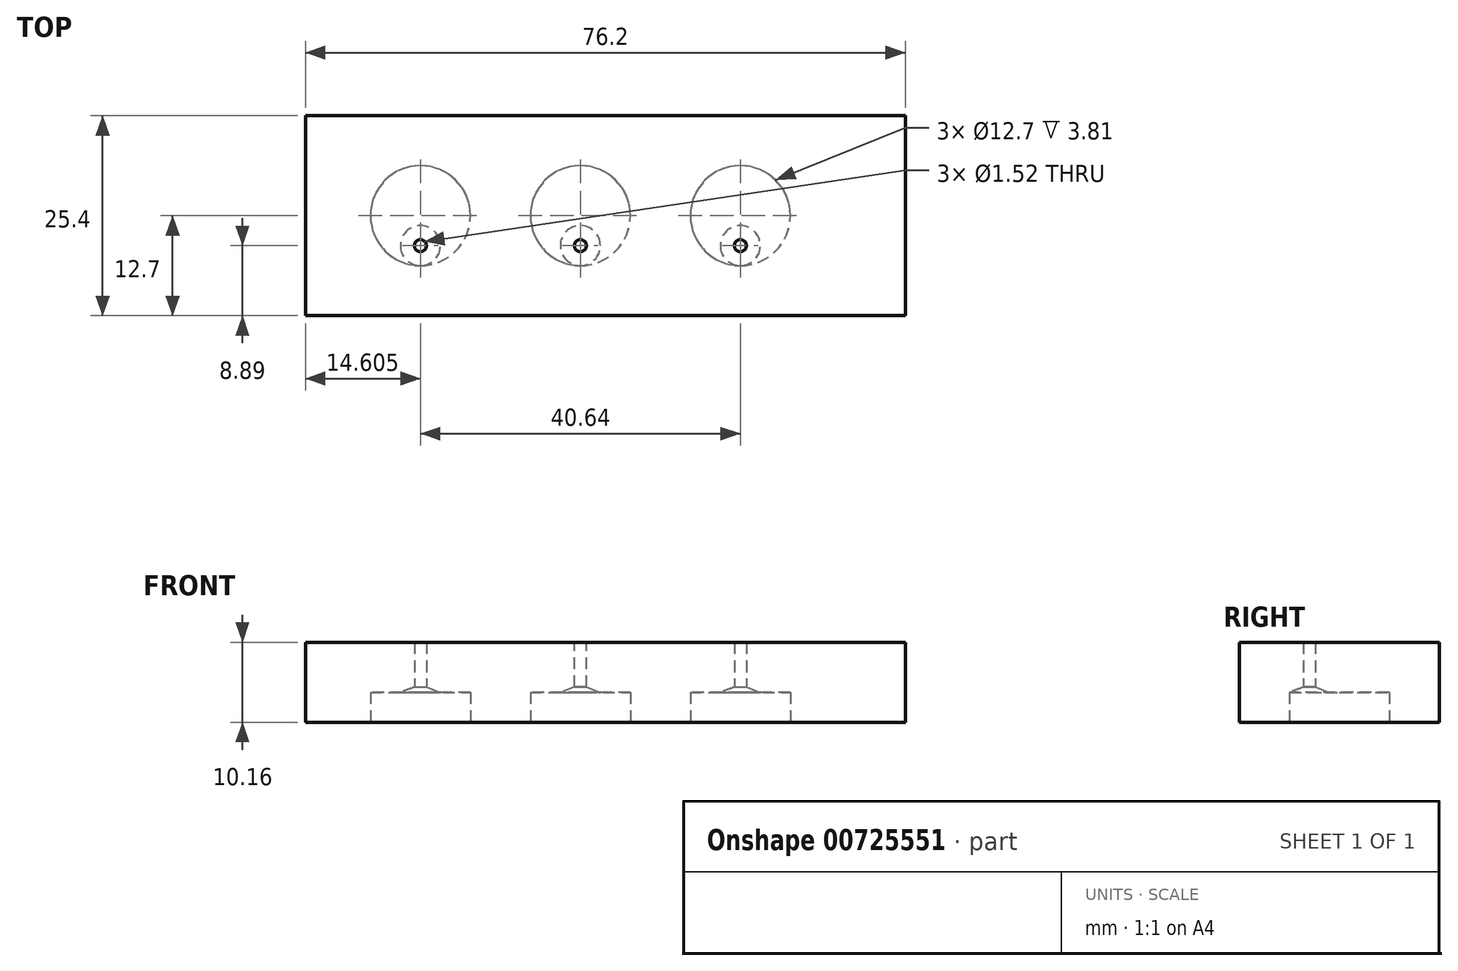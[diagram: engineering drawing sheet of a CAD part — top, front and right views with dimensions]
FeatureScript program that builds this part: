
annotation { "Feature Type Name" : "Feature", "Feature Type Description" : "" }
export const myFeature = defineFeature(function(context is Context, id is Id, definition is map)
    precondition{}
    {
        {
            var Q0;
            Q0=qCreatedBy(makeId("Top.planeOp"),FACE);
            var sketch = newSketch(context, id + "F0", { "sketchPlane" : qUnion([Q0])});
            skLineSegment(sketch, "E0.bottom", {"start": v(38.1, -12.7) * mm, "end": v(-38.1, -12.7) * mm});
            skLineSegment(sketch, "E0.top", {"start": v(38.1, 12.7) * mm, "end": v(-38.1, 12.7) * mm});
            skLineSegment(sketch, "E0.left", {"start": v(38.1, -12.7) * mm, "end": v(38.1, 12.7) * mm});
            skLineSegment(sketch, "E0.right", {"start": v(-38.1, -12.7) * mm, "end": v(-38.1, 12.7) * mm});
            skPoint(sketch, "E0.middle", {"position": v(0, 0) * mm});
            skSolve(sketch);
        }
        {
            var Q0;
            Q0=makeQuery(id+"F0.imprint","IMPRINT",FACE,{"disambiguationData":[TD([[makeQuery(id+"F0.imprint","IMPRINT",EDGE,{"derivedFrom":sQuery(id+"F0.wireOp",EDGE,"E0.bottom")}),-1.0]])]});
            extrude(context, id + "F1", {"entities" : qUnion([Q0]), "depth" : 10.16 * mm, "offsetDistance" : 25.4 * mm});
        }
        {
            var Q0;
            Q0=makeQuery(id+"F1.opExtrude","CAP_FACE",FACE,{"disambiguationData":[OSD([sQuery(id+"F0.wireOp",EDGE,"E0.bottom"),sQuery(id+"F0.wireOp",EDGE,"E0.top"),sQuery(id+"F0.wireOp",EDGE,"E0.left"),sQuery(id+"F0.wireOp",EDGE,"E0.right")])],"isStart":true});
            var sketch = newSketch(context, id + "F2", { "sketchPlane" : qUnion([Q0])});
            skCircle(sketch, "E1", {"center": v(-3.18, 0) * mm, "radius": 6.35 * mm});
            skCircle(sketch, "E2", {"center": v(-23.5, 0) * mm, "radius": 6.35 * mm});
            skCircle(sketch, "E3", {"center": v(17.15, 0) * mm, "radius": 6.35 * mm});
            skSolve(sketch);
        }
        {
            var Q0;
            Q0=makeQuery(id+"F2.imprint","IMPRINT",FACE,{"disambiguationData":[TD([[makeQuery(id+"F2.imprint","IMPRINT",EDGE,{"derivedFrom":sQuery(id+"F2.wireOp",EDGE,"E2")}),1.0]])]});
            var Q1;
            Q1=makeQuery(id+"F2.imprint","IMPRINT",FACE,{"disambiguationData":[TD([[makeQuery(id+"F2.imprint","IMPRINT",EDGE,{"derivedFrom":sQuery(id+"F2.wireOp",EDGE,"E1")}),1.0]])]});
            var Q2;
            Q2=makeQuery(id+"F2.imprint","IMPRINT",FACE,{"disambiguationData":[TD([[makeQuery(id+"F2.imprint","IMPRINT",EDGE,{"derivedFrom":sQuery(id+"F2.wireOp",EDGE,"E3")}),1.0]])]});
            extrude(context, id + "F3", {"entities" : qUnion([Q0, Q1, Q2]), "operationType" : NewBodyOperationType.REMOVE, "oppositeDirection" : true, "depth" : 3.8 * mm, "offsetDistance" : 25.4 * mm});
        }
        {
            var Q0;
            Q0=makeQuery(id+"F1.opExtrude","SWEPT_FACE",FACE,{"disambiguationData":[OSD([sQuery(id+"F0.wireOp",EDGE,"E0.bottom")])]});
            cPlane(context, id + "F4", {"entities" : qUnion([Q0]), "cplaneType" : CPlaneType.OFFSET, "offset" : 8.9 * mm, "oppositeDirection" : true, "width" : 152.4 * mm, "height" : 152.4 * mm});
        }
        {
            var Q0;
            Q0=qCreatedBy(id+"F4.planeOp",FACE);
            var sketch = newSketch(context, id + "F5", { "sketchPlane" : qUnion([Q0])});
            skLineSegment(sketch, "E4.0", {"start": v(-17.15, 3.81) * mm, "end": v(-29.85, 3.81) * mm});
            skLineSegment(sketch, "E5", {"start": v(-23.5, 3.81) * mm, "end": v(-23.5, 8.21) * mm, "construction": true});
            skLineSegment(sketch, "E6", {"start": v(-23.5, 3.81) * mm, "end": v(-26.04, 3.81) * mm});
            skLineSegment(sketch, "E7", {"start": v(-26.04, 3.81) * mm, "end": v(-24.26, 4.46) * mm});
            skLineSegment(sketch, "E8", {"start": v(-24.26, 4.46) * mm, "end": v(-24.26, 10.42) * mm});
            skLineSegment(sketch, "E9", {"start": v(-24.26, 10.42) * mm, "end": v(-23.5, 10.42) * mm});
            skLineSegment(sketch, "E10", {"start": v(-23.5, 10.42) * mm, "end": v(-23.5, 3.81) * mm});
            skSolve(sketch);
        }
        {
            var Q0;
            Q0 = qSketchRegion(id + "F5", true);
            var Q1;
            Q1=sQuery(id+"F5.wireOp",EDGE,"E10");
            revolve(context, id + "F6", {"operationType" : NewBodyOperationType.REMOVE, "surfaceOperationType" : NewSurfaceOperationType.NEW, "entities" : qUnion([Q0]), "axis" : qUnion([Q1]), "revolveType" : RevolveType.FULL, "oppositeDirection" : true});
        }
        {
            var Q0;
            Q0=qCreatedBy(id+"F4.planeOp",FACE);
            var sketch = newSketch(context, id + "F7", { "sketchPlane" : qUnion([Q0])});
            skLineSegment(sketch, "E11.0", {"start": v(3.18, 3.81) * mm, "end": v(-9.53, 3.81) * mm});
            skLineSegment(sketch, "E12", {"start": v(-3.18, 3.81) * mm, "end": v(-3.18, 16.28) * mm, "construction": true});
            skLineSegment(sketch, "E13", {"start": v(-3.18, 16.28) * mm, "end": v(-3.18, 14.18) * mm, "construction": true});
            skLineSegment(sketch, "E14.0", {"start": v(3.18, 3.8) * mm, "end": v(-9.53, 3.8) * mm});
            skLineSegment(sketch, "E15", {"start": v(-3.17, 3.8) * mm, "end": v(-3.17, 8.21) * mm, "construction": true});
            skLineSegment(sketch, "E16", {"start": v(-3.17, 3.8) * mm, "end": v(-5.71, 3.8) * mm});
            skLineSegment(sketch, "E17", {"start": v(-5.71, 3.8) * mm, "end": v(-3.94, 4.46) * mm});
            skLineSegment(sketch, "E18", {"start": v(-3.94, 4.46) * mm, "end": v(-3.94, 10.42) * mm});
            skLineSegment(sketch, "E19", {"start": v(-3.94, 10.42) * mm, "end": v(-3.17, 10.42) * mm});
            skLineSegment(sketch, "E20", {"start": v(-3.17, 10.42) * mm, "end": v(-3.17, 3.8) * mm});
            skSolve(sketch);
        }
        {
            var Q0;
            Q0 = qSketchRegion(id + "F7", true);
            var Q1;
            Q1=sQuery(id+"F7.wireOp",EDGE,"E12");
            revolve(context, id + "F8", {"operationType" : NewBodyOperationType.REMOVE, "surfaceOperationType" : NewSurfaceOperationType.NEW, "entities" : qUnion([Q0]), "axis" : qUnion([Q1]), "revolveType" : RevolveType.FULL, "oppositeDirection" : true});
        }
        {
            var Q0;
            Q0=qCreatedBy(id+"F4.planeOp",FACE);
            var sketch = newSketch(context, id + "F9", { "sketchPlane" : qUnion([Q0])});
            skLineSegment(sketch, "E21.0", {"start": v(23.5, 3.81) * mm, "end": v(10.8, 3.81) * mm});
            skLineSegment(sketch, "E22", {"start": v(17.15, 3.81) * mm, "end": v(17.15, 12.26) * mm, "construction": true});
            skLineSegment(sketch, "E23.0", {"start": v(23.47, 3.81) * mm, "end": v(10.82, 3.81) * mm});
            skLineSegment(sketch, "E24", {"start": v(17.15, 3.81) * mm, "end": v(17.15, 16.28) * mm, "construction": true});
            skLineSegment(sketch, "E25", {"start": v(17.15, 16.28) * mm, "end": v(17.15, 14.18) * mm, "construction": true});
            skLineSegment(sketch, "E26.0", {"start": v(23.47, 3.81) * mm, "end": v(10.82, 3.8) * mm});
            skLineSegment(sketch, "E27", {"start": v(17.15, 3.81) * mm, "end": v(17.15, 8.21) * mm, "construction": true});
            skLineSegment(sketch, "E28", {"start": v(17.15, 3.81) * mm, "end": v(14.6, 3.8) * mm});
            skLineSegment(sketch, "E29", {"start": v(14.6, 3.8) * mm, "end": v(16.38, 4.46) * mm});
            skLineSegment(sketch, "E30", {"start": v(16.38, 4.46) * mm, "end": v(16.38, 10.42) * mm});
            skLineSegment(sketch, "E31", {"start": v(16.38, 10.42) * mm, "end": v(17.15, 10.42) * mm});
            skLineSegment(sketch, "E32", {"start": v(17.15, 10.42) * mm, "end": v(17.15, 3.81) * mm});
            skSolve(sketch);
        }
        {
            var Q0;
            Q0 = qSketchRegion(id + "F9", true);
            var Q1;
            Q1=sQuery(id+"F9.wireOp",EDGE,"E22");
            revolve(context, id + "F10", {"operationType" : NewBodyOperationType.REMOVE, "surfaceOperationType" : NewSurfaceOperationType.NEW, "entities" : qUnion([Q0]), "axis" : qUnion([Q1]), "revolveType" : RevolveType.FULL});
        }
    });
